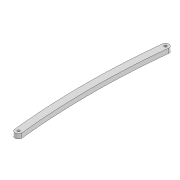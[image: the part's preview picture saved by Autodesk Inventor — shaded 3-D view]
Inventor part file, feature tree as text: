
AUTODESK INVENTOR PART (.ipt)
format: ipt  version: 2022 (Build 260153000, 153)  size: 93,696 bytes
history: native  units: mm
features: extrude x1, sketch x1
ambient origin geometry x8: Origin, YZ Plane, XZ Plane, XY Plane, X Axis, Y Axis, Z Axis, Center Point
bodies: Solid1 (feature_tree)
feature tree (2):
  extrude  "Extrusion1"  Depth=600.0mm
  sketch  "Sketch1"  dims[d0=2.2mm d1=2.2mm d2=6.0mm d3=128.331mm d6=4.0mm d7=0.0mm d14=600.0mm d15=600.0mm]
